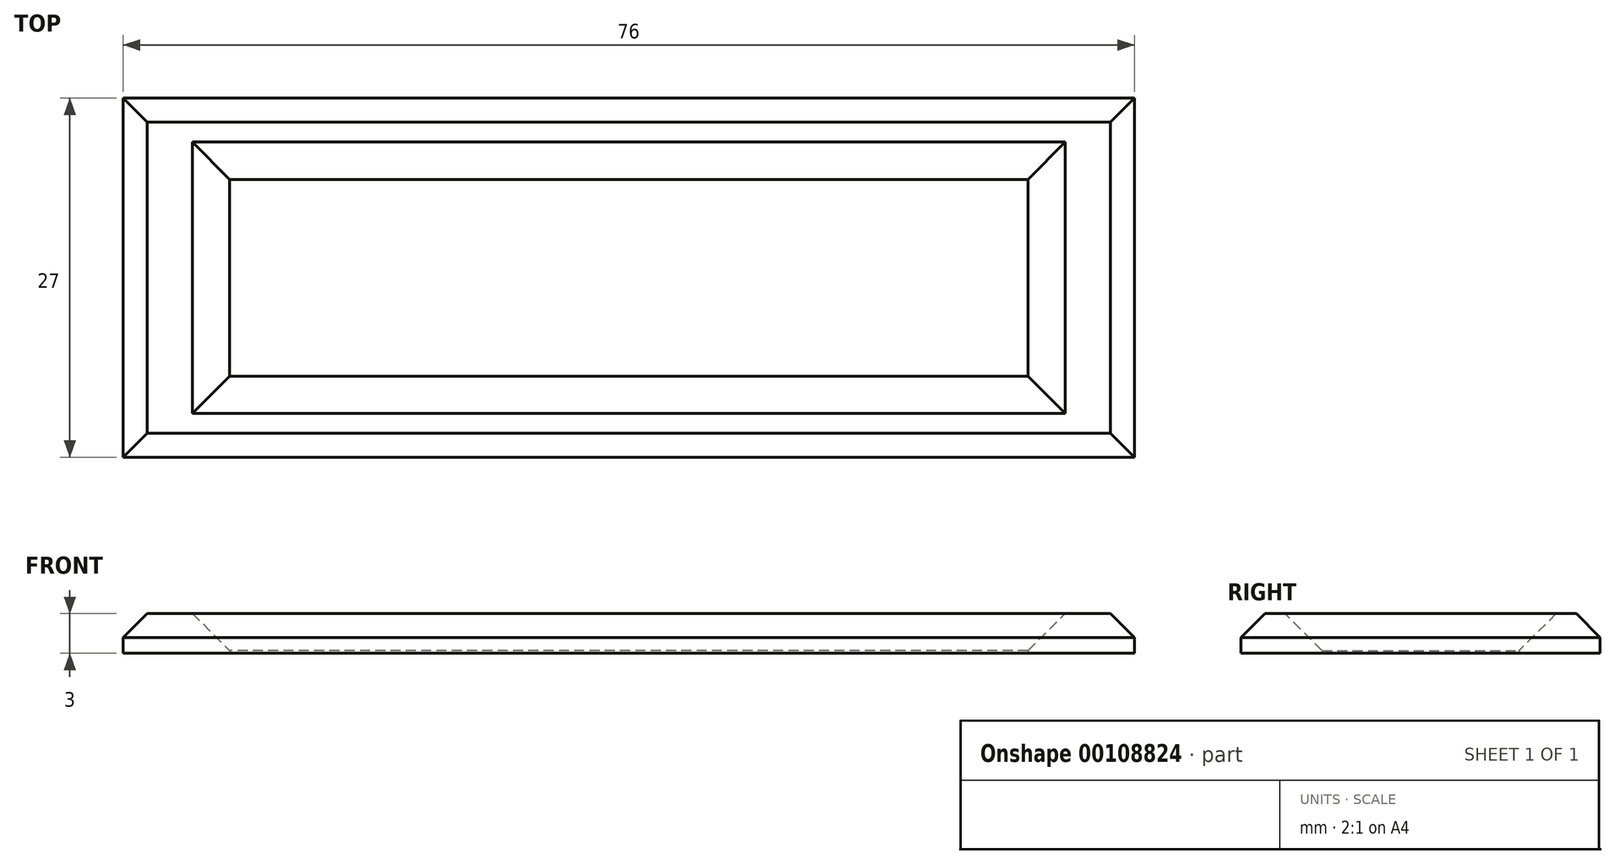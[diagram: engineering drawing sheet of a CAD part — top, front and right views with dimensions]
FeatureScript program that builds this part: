
annotation { "Feature Type Name" : "Feature", "Feature Type Description" : "" }
export const myFeature = defineFeature(function(context is Context, id is Id, definition is map)
    precondition{}
    {
        {
            var Q0;
            Q0=qCreatedBy(makeId("Top.planeOp"),FACE);
            var sketch = newSketch(context, id + "F0", { "sketchPlane" : qUnion([Q0])});
            skLineSegment(sketch, "E0.bottom", {"start": v(-38, 13.5) * mm, "end": v(38, 13.5) * mm});
            skLineSegment(sketch, "E0.top", {"start": v(-38, -13.5) * mm, "end": v(38, -13.5) * mm});
            skLineSegment(sketch, "E0.left", {"start": v(-38, 13.5) * mm, "end": v(-38, -13.5) * mm});
            skLineSegment(sketch, "E0.right", {"start": v(38, 13.5) * mm, "end": v(38, -13.5) * mm});
            skPoint(sketch, "E0.middle", {"position": v(0, 0) * mm});
            skLineSegment(sketch, "E1.bottom", {"start": v(30, 7.4) * mm, "end": v(-30, 7.4) * mm});
            skLineSegment(sketch, "E1.top", {"start": v(30, -7.4) * mm, "end": v(-30, -7.4) * mm});
            skLineSegment(sketch, "E1.left", {"start": v(30, 7.4) * mm, "end": v(30, -7.4) * mm});
            skLineSegment(sketch, "E1.right", {"start": v(-30, 7.4) * mm, "end": v(-30, -7.4) * mm});
            skSolve(sketch);
        }
        {
            var Q0;
            Q0 = qSketchRegion(id + "F0", true);
            extrude(context, id + "F1", {"entities" : qUnion([Q0]), "depth" : 3 * mm, "offsetDistance" : 25 * mm});
        }
        {
            var Q0;
            Q0=makeQuery(id+"F1.opExtrude","CAP_EDGE",EDGE,{"disambiguationData":[OSD([sQuery(id+"F0.wireOp",EDGE,"E1.bottom")])],"isStart":false});
            var Q1;
            Q1=makeQuery(id+"F1.opExtrude","CAP_EDGE",EDGE,{"disambiguationData":[OSD([sQuery(id+"F0.wireOp",EDGE,"E1.left")])],"isStart":false});
            var Q2;
            Q2=makeQuery(id+"F1.opExtrude","CAP_EDGE",EDGE,{"disambiguationData":[OSD([sQuery(id+"F0.wireOp",EDGE,"E1.top")])],"isStart":false});
            var Q3;
            Q3=makeQuery(id+"F1.opExtrude","CAP_EDGE",EDGE,{"disambiguationData":[OSD([sQuery(id+"F0.wireOp",EDGE,"E1.right")])],"isStart":false});
            chamfer(context, id + "F2", {"entities" : qUnion([Q0, Q1, Q2, Q3]), "width" : 2.8 * mm, "tangentPropagation" : true});
        }
        {
            var Q0;
            Q0=makeQuery(id+"F1.opExtrude","CAP_EDGE",EDGE,{"disambiguationData":[OSD([sQuery(id+"F0.wireOp",EDGE,"E0.bottom")])],"isStart":false});
            var Q1;
            Q1=makeQuery(id+"F1.opExtrude","CAP_EDGE",EDGE,{"disambiguationData":[OSD([sQuery(id+"F0.wireOp",EDGE,"E0.left")])],"isStart":false});
            var Q2;
            Q2=makeQuery(id+"F1.opExtrude","CAP_EDGE",EDGE,{"disambiguationData":[OSD([sQuery(id+"F0.wireOp",EDGE,"E0.top")])],"isStart":false});
            var Q3;
            Q3=makeQuery(id+"F1.opExtrude","CAP_EDGE",EDGE,{"disambiguationData":[OSD([sQuery(id+"F0.wireOp",EDGE,"E0.right")])],"isStart":false});
            chamfer(context, id + "F3", {"entities" : qUnion([Q0, Q1, Q2, Q3]), "width" : 1.8 * mm, "tangentPropagation" : true});
        }
    });
